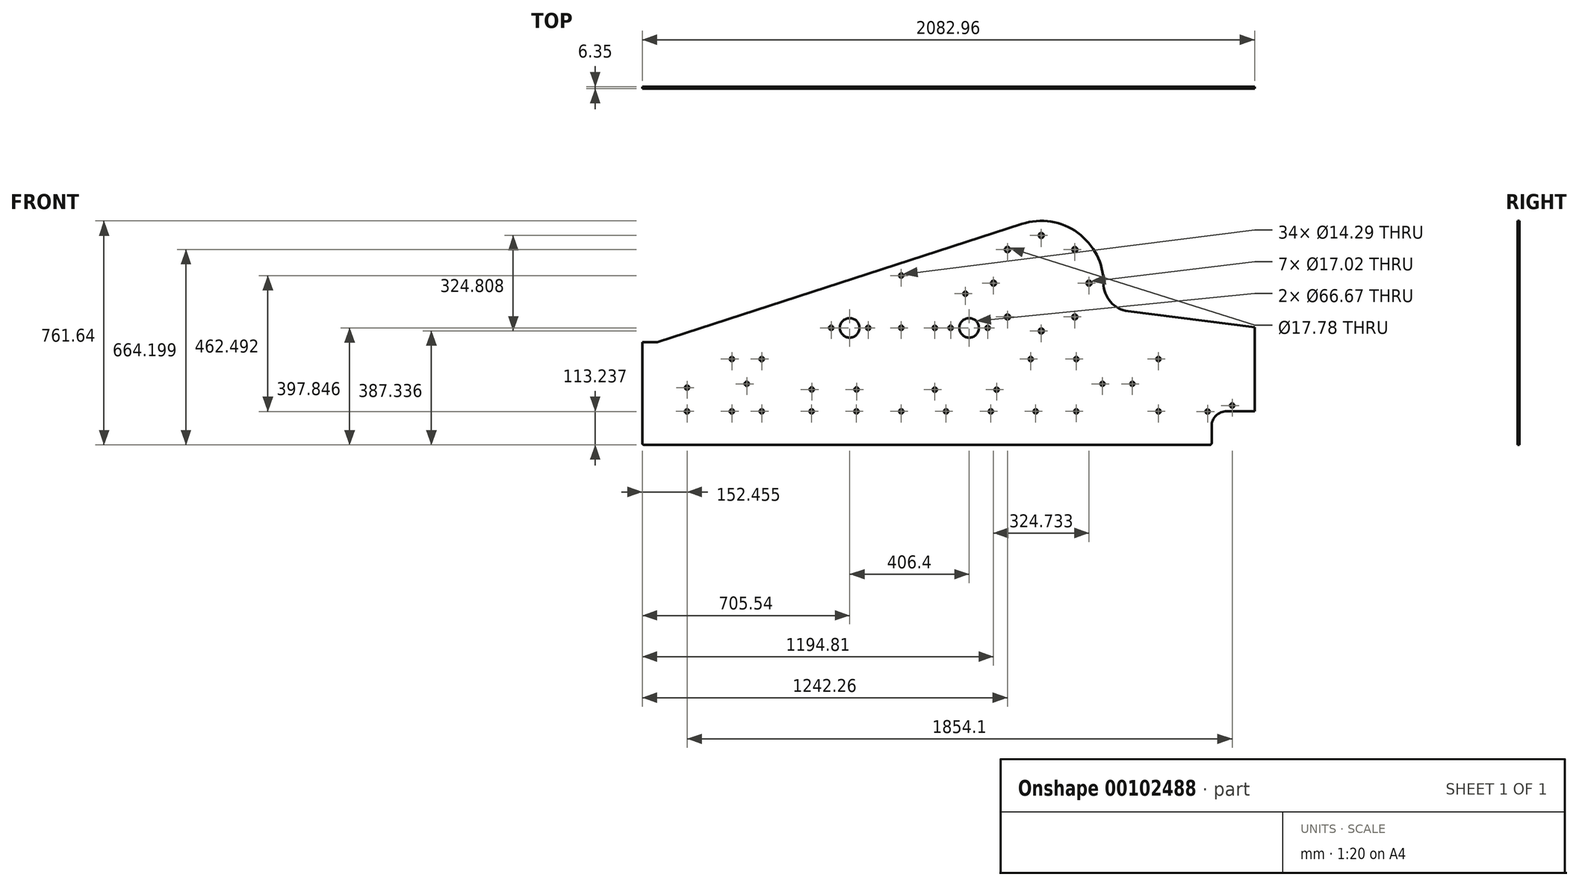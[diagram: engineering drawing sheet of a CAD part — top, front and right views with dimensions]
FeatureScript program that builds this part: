
annotation { "Feature Type Name" : "Feature", "Feature Type Description" : "" }
export const myFeature = defineFeature(function(context is Context, id is Id, definition is map)
    precondition{}
    {
        {
            var Q0;
            Q0=qCreatedBy(makeId("Front.planeOp"),FACE);
            var sketch = newSketch(context, id + "F0", { "sketchPlane" : qUnion([Q0])});
            skCircle(sketch, "E0", {"center": v(70.46, 17.03) * mm, "radius": 33.34 * mm});
            skCircle(sketch, "E1", {"center": v(7.55, 17.03) * mm, "radius": 7.14 * mm});
            skCircle(sketch, "E2", {"center": v(133.37, 17.03) * mm, "radius": 7.14 * mm});
            skCircle(sketch, "E3", {"center": v(-335.94, 17.03) * mm, "radius": 33.34 * mm});
            skCircle(sketch, "E4", {"center": v(-398.85, 17.03) * mm, "radius": 7.14 * mm});
            skCircle(sketch, "E5", {"center": v(-273.03, 17.03) * mm, "radius": 7.14 * mm});
            skCircle(sketch, "E6", {"center": v(434.92, -89.1) * mm, "radius": 7.14 * mm});
            skCircle(sketch, "E7", {"center": v(714.27, -89.15) * mm, "radius": 7.14 * mm});
            skCircle(sketch, "E8", {"center": v(523.81, -173.23) * mm, "radius": 7.14 * mm});
            skCircle(sketch, "E9", {"center": v(625.43, -173.25) * mm, "radius": 7.14 * mm});
            skCircle(sketch, "E10", {"center": v(434.87, -266.86) * mm, "radius": 7.14 * mm});
            skCircle(sketch, "E11", {"center": v(714.33, -266.93) * mm, "radius": 7.14 * mm});
            skCircle(sketch, "E12", {"center": v(-736.59, -89.16) * mm, "radius": 7.14 * mm});
            skCircle(sketch, "E13", {"center": v(-736.62, -267) * mm, "radius": 7.14 * mm});
            skCircle(sketch, "E14", {"center": v(-635.07, -266.93) * mm, "radius": 7.14 * mm});
            skCircle(sketch, "E15", {"center": v(-685.84, -173.25) * mm, "radius": 7.14 * mm});
            skCircle(sketch, "E16", {"center": v(-635.01, -89.2) * mm, "radius": 7.14 * mm});
            skCircle(sketch, "E17", {"center": v(-160.5, -266.9) * mm, "radius": 7.14 * mm});
            skCircle(sketch, "E18", {"center": v(-160.48, 17.03) * mm, "radius": 7.14 * mm});
            skCircle(sketch, "E19", {"center": v(-160.5, 194.9) * mm, "radius": 7.14 * mm});
            skArc(sketch, "E20", {"start": v(946.07, -266.52) * mm, "mid": v(910.15, -281.4) * mm, "end": v(895.27, -317.32) * mm, "construction": true});
            skArc(sketch, "E21", {"start": v(-1041.48, -374.47) * mm, "mid": v(-1039.62, -378.96) * mm, "end": v(-1035.13, -380.82) * mm, "construction": true});
            skArc(sketch, "E22", {"start": v(888.92, -380.82) * mm, "mid": v(893.41, -378.96) * mm, "end": v(895.27, -374.47) * mm, "construction": true});
            skArc(sketch, "E23", {"start": v(527.33, 168.92) * mm, "mid": v(551.32, 105.45) * mm, "end": v(611.3, 73.73) * mm, "construction": true});
            skArc(sketch, "E24", {"start": v(527.33, 168.92) * mm, "mid": v(439.97, 340.32) * mm, "end": v(249.97, 370.5) * mm, "construction": true});
            skLineSegment(sketch, "E25", {"start": v(-1041.48, -31.57) * mm, "end": v(-990.68, -31.57) * mm, "construction": true});
            skCircle(sketch, "E26", {"center": v(279.97, -89.12) * mm, "radius": 7.14 * mm});
            skCircle(sketch, "E27", {"center": v(57.56, 133.14) * mm, "radius": 7.14 * mm});
            skCircle(sketch, "E28", {"center": v(-46.4, 17.03) * mm, "radius": 7.14 * mm});
            skCircle(sketch, "E29", {"center": v(163.92, -193.15) * mm, "radius": 7.14 * mm});
            skCircle(sketch, "E30", {"center": v(-8.1, -266.9) * mm, "radius": 7.14 * mm});
            skCircle(sketch, "E31", {"center": v(144.3, -266.9) * mm, "radius": 7.14 * mm});
            skCircle(sketch, "E32", {"center": v(296.7, -266.9) * mm, "radius": 7.14 * mm});
            skCircle(sketch, "E33", {"center": v(-312.9, -266.9) * mm, "radius": 7.14 * mm});
            skCircle(sketch, "E34", {"center": v(-465.3, -266.9) * mm, "radius": 7.14 * mm});
            skCircle(sketch, "E35", {"center": v(-889.02, -267) * mm, "radius": 7.14 * mm});
            skCircle(sketch, "E36", {"center": v(-888.89, -186.2) * mm, "radius": 7.14 * mm});
            skCircle(sketch, "E37", {"center": v(-465.01, -192.54) * mm, "radius": 7.14 * mm});
            skCircle(sketch, "E38", {"center": v(-312.61, -192.54) * mm, "radius": 7.14 * mm});
            skCircle(sketch, "E39", {"center": v(881.4, -267.58) * mm, "radius": 7.14 * mm});
            skCircle(sketch, "E40", {"center": v(965.08, -247.15) * mm, "radius": 7.14 * mm});
            skLineSegment(sketch, "E41", {"start": v(1041.48, -266.52) * mm, "end": v(1041.48, 19.63) * mm, "construction": true});
            skCircle(sketch, "E42", {"center": v(-46.4, -193.15) * mm, "radius": 7.14 * mm});
            skCircle(sketch, "E43", {"center": v(200.78, 283.38) * mm, "radius": 8.9 * mm});
            skCircle(sketch, "E44", {"center": v(315.72, 331.32) * mm, "radius": 8.5 * mm});
            skCircle(sketch, "E45", {"center": v(429.93, 283.41) * mm, "radius": 8.5 * mm});
            skCircle(sketch, "E46", {"center": v(153.32, 169) * mm, "radius": 8.5 * mm});
            skCircle(sketch, "E47", {"center": v(478.06, 169) * mm, "radius": 8.5 * mm});
            skCircle(sketch, "E48", {"center": v(200.85, 54.2) * mm, "radius": 8.5 * mm});
            skCircle(sketch, "E49", {"center": v(315.8, 6.52) * mm, "radius": 8.5 * mm});
            skCircle(sketch, "E50", {"center": v(429.83, 54.2) * mm, "radius": 8.5 * mm});
            skLineSegment(sketch, "E51", {"start": v(-1041.48, -31.57) * mm, "end": v(-990.68, -31.57) * mm});
            skLineSegment(sketch, "E52", {"start": v(-990.68, -31.57) * mm, "end": v(249.97, 370.5) * mm});
            skArc(sketch, "E53", {"start": v(249.97, 370.5) * mm, "mid": v(439.97, 340.32) * mm, "end": v(527.33, 168.92) * mm});
            skArc(sketch, "E54", {"start": v(611.3, 73.73) * mm, "mid": v(551.31, 105.47) * mm, "end": v(527.33, 168.96) * mm});
            skLineSegment(sketch, "E55", {"start": v(611.3, 73.73) * mm, "end": v(1041.48, 19.63) * mm});
            skLineSegment(sketch, "E56", {"start": v(1041.48, 19.63) * mm, "end": v(1041.48, -266.52) * mm});
            skLineSegment(sketch, "E57", {"start": v(1041.48, -266.52) * mm, "end": v(946.07, -266.52) * mm});
            skArc(sketch, "E58", {"start": v(946.07, -266.52) * mm, "mid": v(910.15, -281.4) * mm, "end": v(895.27, -317.32) * mm});
            skLineSegment(sketch, "E59", {"start": v(895.27, -317.32) * mm, "end": v(895.27, -374.47) * mm});
            skLineSegment(sketch, "E60", {"start": v(888.92, -380.82) * mm, "end": v(-1035.13, -380.82) * mm});
            skArc(sketch, "E61", {"start": v(-1035.13, -380.82) * mm, "mid": v(-1039.62, -378.96) * mm, "end": v(-1041.48, -374.47) * mm});
            skLineSegment(sketch, "E62", {"start": v(-1041.48, -374.47) * mm, "end": v(-1041.48, -31.57) * mm});
            skArc(sketch, "E63", {"start": v(895.27, -374.47) * mm, "mid": v(893.41, -378.96) * mm, "end": v(888.92, -380.82) * mm});
            skSolve(sketch);
        }
        {
            var Q0;
            Q0 = qSketchRegion(id + "F0", true);
            extrude(context, id + "F1", {"entities" : qUnion([Q0]), "depth" : 6.35 * mm});
        }
    });
